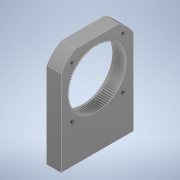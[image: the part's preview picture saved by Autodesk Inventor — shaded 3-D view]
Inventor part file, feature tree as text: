
AUTODESK INVENTOR PART (.ipt)
format: ipt  version: 2022 (Build 260153000, 153)  size: 687,104 bytes
history: mixed  units: in
note: dims shown in document units (in); Inventor stores cm internally (conversion verified against a paired STEP export)
features: sketch x7, extrude x6, other x1, imported_body x1
ambient origin geometry x8: Origin, YZ Plane, XZ Plane, XY Plane, X Axis, Y Axis, Z Axis, Center Point
bodies: Solid1 (imported_parasolid)
feature tree (15):
  extrude  "Extrusion1"  Depth=0.3937in TaperAngle=0.0deg
  extrude  "Extrusion2"  Depth=0.3937in
  extrude  "Extrusion3"  Depth=0.1181in
  sketch  "Sketch5"  dims[d10=0.0in d11=0.0in d12=0.315in d13=0.0in]
  extrude  "Extrusion4"  Depth=0.315in TaperAngle=0.0deg
  extrude  "Extrusion5"  TaperAngle=0.0deg  [1 undecoded]
  extrude  "Extrusion6"  [1 undecoded]
  sketch  "Sketch2"  dims[d1=0.2756in d2=0.0in d3=0.3937in d4=0.0in]
  sketch  "Sketch3"  dims[d5=0.3937in d6=0.0in d7=0.1181in]
  sketch  "Sketch4"  dims[d8=0.1181in d9=0.1181in]
  sketch  "Sketch6"  dims[d14=1.378in d15=0.0in d16=0.0in]
  sketch  "Sketch7"
  sketch  "Sketch8"
  other  "96_Teeth_Gear.STEP"
  imported_body  NMx_Import_Brep_tag  [imported B-rep: ~397 faces, bbox_mm=[12.0, 83.027756, 60.0]]
note: 2 required parameter values undecoded (feature->parameter linkage not recoverable at this tier; creation-order binding heuristic only, values carry confidence <= 0.55)
